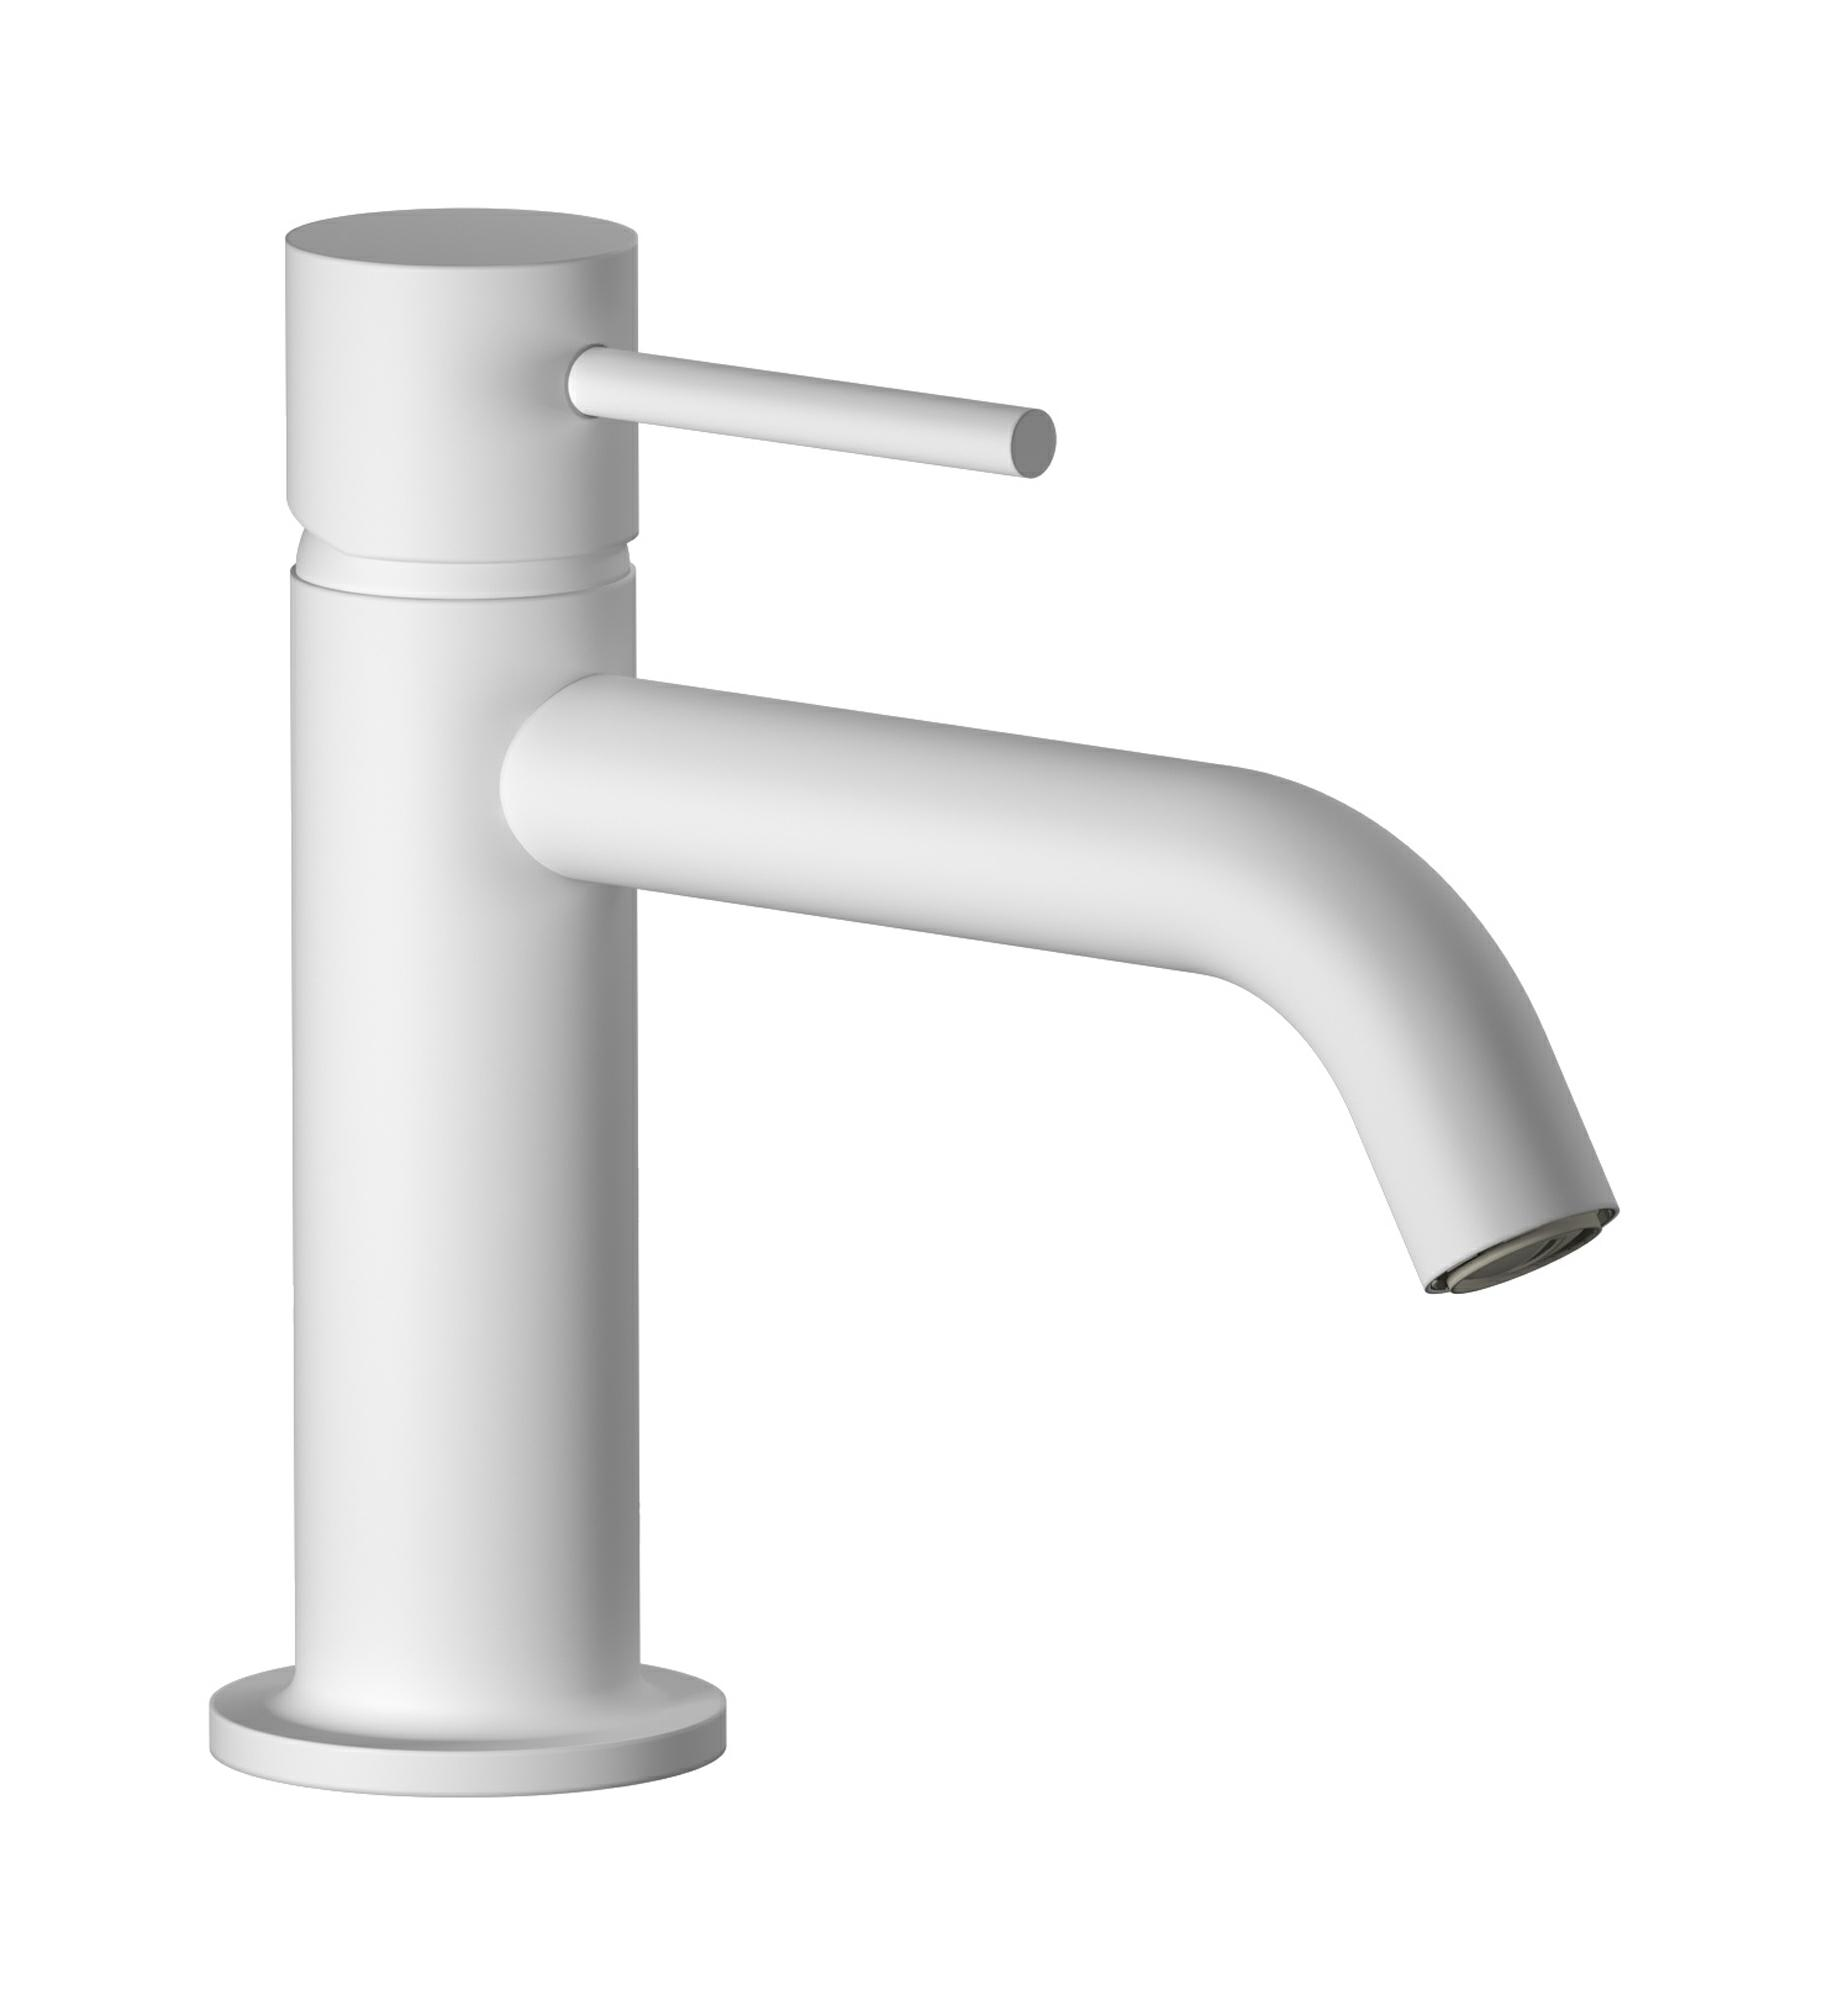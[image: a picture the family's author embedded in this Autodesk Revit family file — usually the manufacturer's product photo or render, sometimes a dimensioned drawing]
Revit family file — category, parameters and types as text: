
# Revit family: MT201
name_source: partatom
category: Apparecchi idraulici
units: mm (PartAtom-declared; Revit-internal decimal feet)

## family parameters
Basato su piano di lavoro = No
Condiviso = No
Mantieni orientamento annotazione = No
Numero OmniClass = 23.45.55.17
Punto di calcolo locali = No
Quota connettore circolare = Usa diametro
Sempre verticale = Sì
Taglio con vuoti quando caricato = No
Tipo di parte = Normale
Titolo OmniClass = Mixing Faucets

## types (13) — shared parameters
Cold water inlet = 10 mm  [stored 0.0328084 ft]
Commenti sul tipo = Washbasin mixer
Connessione CW = No
Connessione HW = No
Connessione di scarico = No
Connessione di ventilazione = No
Descrizione = Mini monohole washbasin mixer complete with drain
Hot water inlet = 10 mm  [stored 0.0328084 ft]
Produttore = IB Rubinetterie S.p.A.
URL = https://www.weareib.it
zero-valued in all types: Prospetto di default

## per-type parameters (varying)
| type | Finishes surface | Immagine tipo | Modello |
| Chrome | IB_Chrome | MT201CC.jpg | MT201CC |
| Brushed nickel | IB_Brushed nickel | MT201SS.jpg | MT201SS |
| Matt black | IB_matt black | MT201NP.jpg | MT201NP |
| Matt white | IB_matt white | MT201BO.jpg | MT201BO |
| Natural brass | IB_Brass | MT201ON.jpg | MT201ON |
| Black chrome | IB_Black chrome | MT201CF.jpg | MT201CF |
| Brushed black chrome | IB_Brushed black chrome | MT201CS.jpg | MT201CS |
| Pale gold | IB_Pale gold | MT201II.jpg | MT201II |
| Brushed pale gold | IB_brushed pale gold | MT201IS.jpg | MT201IS |
| Rose gold | IB_Rose gold | MT201RS.jpg | MT201RS |
| Brushed rose gold | IB_Brushed rose gold | MT201SR.jpg | MT201SR |
| Gold | IB_gold | MT201OO.jpg | MT201OO |
| Brushed gold | IB_brushed gold | MT201OS.jpg | MT201OS |

note: [stored X ft] marks values corroborated as IEEE doubles in the binary element streams (Revit-internal decimal feet)
